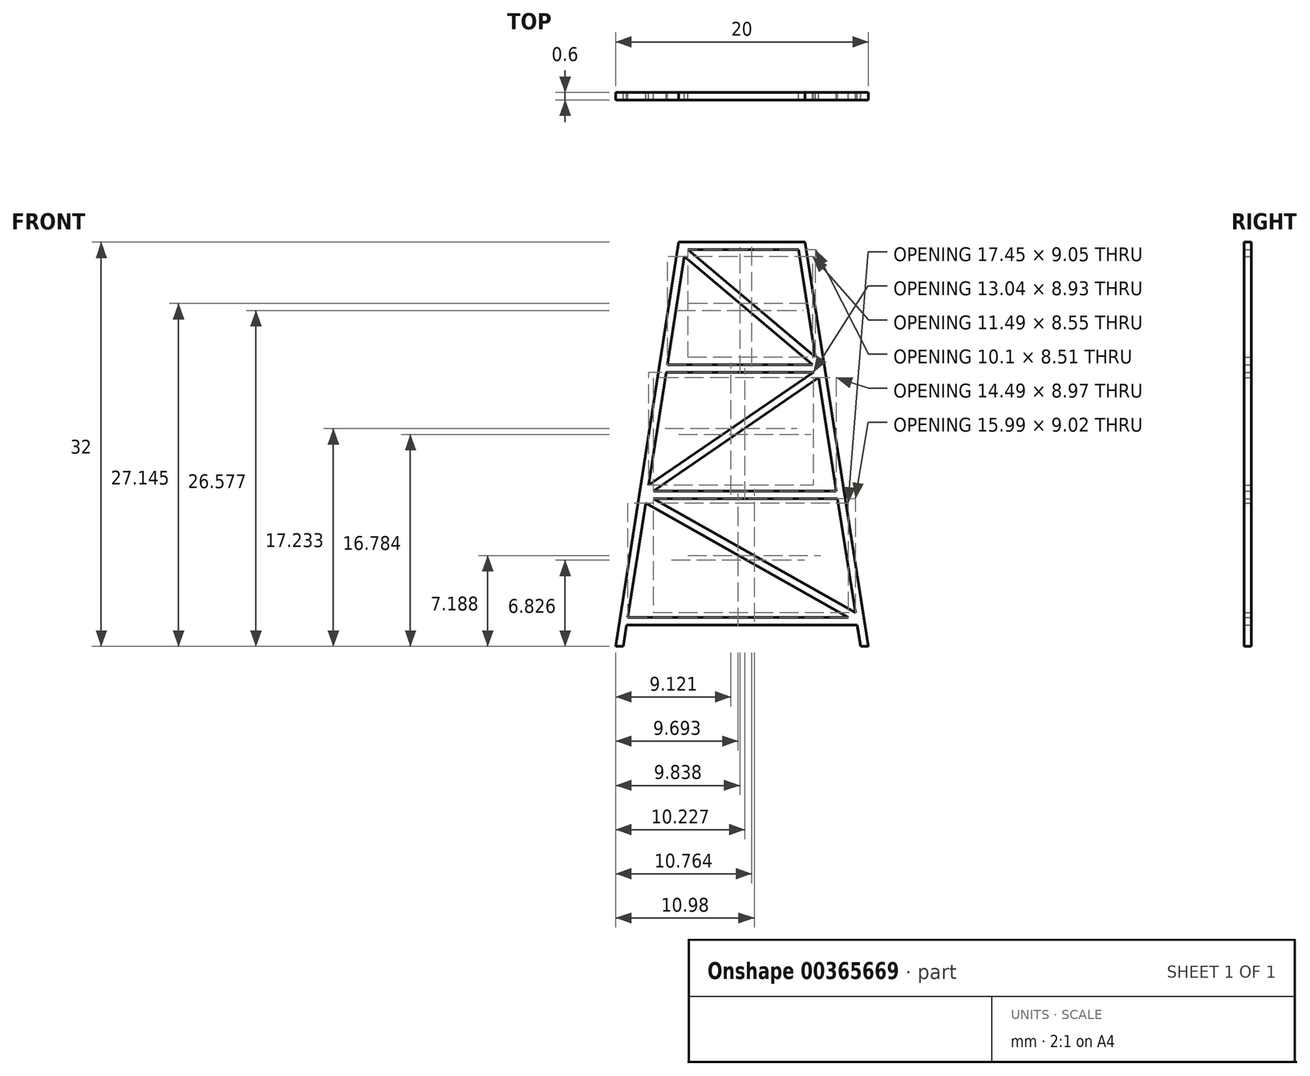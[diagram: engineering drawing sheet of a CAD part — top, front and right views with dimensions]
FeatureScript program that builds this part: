
annotation { "Feature Type Name" : "Feature", "Feature Type Description" : "" }
export const myFeature = defineFeature(function(context is Context, id is Id, definition is map)
    precondition{}
    {
        {
            var Q0;
            Q0=qCreatedBy(makeId("Front.planeOp"),FACE);
            var sketch = newSketch(context, id + "F0", { "sketchPlane" : qUnion([Q0])});
            skLineSegment(sketch, "E0", {"start": v(0, 0) * mm, "end": v(0, 32) * mm});
            skLineSegment(sketch, "E1", {"start": v(0, 32) * mm, "end": v(5, 32) * mm});
            skPoint(sketch, "E2", {"position": v(0, 0) * mm});
            skPoint(sketch, "E3", {"position": v(10, 0) * mm});
            skLineSegment(sketch, "E4", {"start": v(5, 32) * mm, "end": v(10, 0) * mm});
            skLineSegment(sketch, "E5", {"start": v(0, 31.4) * mm, "end": v(4.49, 31.4) * mm});
            skLineSegment(sketch, "E6", {"start": v(4.49, 31.4) * mm, "end": v(9.4, 0) * mm});
            skPoint(sketch, "E7", {"position": v(0, 2) * mm});
            skPoint(sketch, "E8", {"position": v(0, 12) * mm});
            skPoint(sketch, "E9", {"position": v(0, 22) * mm});
            skPoint(sketch, "E10", {"position": v(0, 22.3) * mm});
            skPoint(sketch, "E11", {"position": v(0, 21.7) * mm});
            skPoint(sketch, "E12", {"position": v(0, 12.3) * mm});
            skPoint(sketch, "E13", {"position": v(0, 11.7) * mm});
            skPoint(sketch, "E14", {"position": v(0, 2.3) * mm});
            skPoint(sketch, "E15", {"position": v(0, 1.7) * mm});
            skLineSegment(sketch, "E16", {"start": v(0, 22.3) * mm, "end": v(6.52, 22.3) * mm});
            skLineSegment(sketch, "E17", {"start": v(0, 21.7) * mm, "end": v(6, 21.7) * mm});
            skLineSegment(sketch, "E18", {"start": v(0, 12.3) * mm, "end": v(8.08, 12.3) * mm});
            skLineSegment(sketch, "E19", {"start": v(0, 11.7) * mm, "end": v(7.56, 11.7) * mm});
            skLineSegment(sketch, "E20", {"start": v(0, 2.3) * mm, "end": v(9.64, 2.3) * mm});
            skLineSegment(sketch, "E21", {"start": v(0, 1.7) * mm, "end": v(9.13, 1.7) * mm});
            skLineSegment(sketch, "E22.MirrorCS", {"start": v(0, 31.4) * mm, "end": v(-4.49, 31.4) * mm});
            skLineSegment(sketch, "E23.MirrorCS", {"start": v(0, 32) * mm, "end": v(-5, 32) * mm});
            skLineSegment(sketch, "E24.MirrorCS", {"start": v(-4.49, 31.4) * mm, "end": v(-9.4, 0) * mm});
            skLineSegment(sketch, "E25.MirrorCS", {"start": v(-5, 32) * mm, "end": v(-10, 0) * mm});
            skLineSegment(sketch, "E26.MirrorCS", {"start": v(0, 22.3) * mm, "end": v(-6.52, 22.3) * mm});
            skLineSegment(sketch, "E27.MirrorCS", {"start": v(0, 21.7) * mm, "end": v(-6, 21.7) * mm});
            skLineSegment(sketch, "E28.MirrorCS", {"start": v(0, 12.3) * mm, "end": v(-8.08, 12.3) * mm});
            skLineSegment(sketch, "E29.MirrorCS", {"start": v(0, 11.7) * mm, "end": v(-7.56, 11.7) * mm});
            skLineSegment(sketch, "E30.MirrorCS", {"start": v(0, 2.3) * mm, "end": v(-9.64, 2.3) * mm});
            skLineSegment(sketch, "E31.MirrorCS", {"start": v(0, 1.7) * mm, "end": v(-9.13, 1.7) * mm});
            skLineSegment(sketch, "E32", {"start": v(-5, 32) * mm, "end": v(6.52, 22.3) * mm});
            skLineSegment(sketch, "E33", {"start": v(-4.57, 30.85) * mm, "end": v(5.58, 22.3) * mm});
            skLineSegment(sketch, "E34", {"start": v(6.52, 22.3) * mm, "end": v(-8.08, 12.3) * mm});
            skLineSegment(sketch, "E35", {"start": v(-8.08, 12.3) * mm, "end": v(9.64, 2.3) * mm});
            skLineSegment(sketch, "E36", {"start": v(6.07, 21.27) * mm, "end": v(-7.02, 12.3) * mm});
            skLineSegment(sketch, "E37", {"start": v(-7.62, 11.35) * mm, "end": v(8.42, 2.3) * mm});
            skLineSegment(sketch, "E38", {"start": v(9.4, 0) * mm, "end": v(10, 0) * mm});
            skLineSegment(sketch, "E39", {"start": v(-10, 0) * mm, "end": v(-9.4, 0) * mm});
            skSolve(sketch);
        }
        {
            var Q0;
            {var subQ0=sQuery(id+"F0.wireOp",EDGE,"E39");Q0=makeQuery(id+"F0.imprint","IMPRINT",FACE,{"disambiguationData":[TD([[makeQuery(id+"F0.imprint","IMPRINT",EDGE,{"derivedFrom":subQ0}),1.0]])]});}
            var Q1;
            {var subQ5=sQuery(id+"F0.wireOp",EDGE,"E24.MirrorCS");var subQ8=makeQuery(id+"F0.imprint","INTERSECT",VERTEX,{"derivedFrom":[subQ5,sQuery(id+"F0.wireOp",EDGE,"E29.MirrorCS")]});Q1=makeQuery(id+"F0.imprint","IMPRINT",FACE,{"disambiguationData":[TD([[makeQuery(id+"F0.imprint","IMPRINT",EDGE,{"disambiguationData":[TD([[subQ8,1.0]])],"derivedFrom":subQ5}),-1.0]])]});}
            var Q2;
            {var subQ3=sQuery(id+"F0.wireOp",EDGE,"E24.MirrorCS");var subQ5=makeQuery(id+"F0.imprint","INTERSECT",VERTEX,{"derivedFrom":[subQ3,sQuery(id+"F0.wireOp",EDGE,"E27.MirrorCS")]});Q2=makeQuery(id+"F0.imprint","IMPRINT",FACE,{"disambiguationData":[TD([[makeQuery(id+"F0.imprint","IMPRINT",EDGE,{"disambiguationData":[TD([[subQ5,1.0]])],"derivedFrom":subQ3}),-1.0]])]});}
            var Q3;
            {var subQ5=sQuery(id+"F0.wireOp",EDGE,"E24.MirrorCS");var subQ6=sQuery(id+"F0.wireOp",EDGE,"E22.MirrorCS");var subQ7=makeQuery(id+"F0.imprint","INTERSECT",VERTEX,{"derivedFrom":[subQ6,subQ5]});Q3=makeQuery(id+"F0.imprint","IMPRINT",FACE,{"disambiguationData":[TD([[makeQuery(id+"F0.imprint","IMPRINT",EDGE,{"disambiguationData":[TD([[subQ7,1.0]])],"derivedFrom":subQ6}),-1.0]])]});}
            var Q4;
            {var subQ1=sQuery(id+"F0.wireOp",EDGE,"E1");Q4=makeQuery(id+"F0.imprint","IMPRINT",FACE,{"disambiguationData":[TD([[makeQuery(id+"F0.imprint","IMPRINT",EDGE,{"derivedFrom":subQ1}),-1.0]])]});}
            var Q5;
            {var subQ0=sQuery(id+"F0.wireOp",EDGE,"E23.MirrorCS");Q5=makeQuery(id+"F0.imprint","IMPRINT",FACE,{"disambiguationData":[TD([[makeQuery(id+"F0.imprint","IMPRINT",EDGE,{"derivedFrom":subQ0}),1.0]])]});}
            var Q6;
            {var subQ0=sQuery(id+"F0.wireOp",EDGE,"E6");var subQ4=makeQuery(id+"F0.imprint","INTERSECT",VERTEX,{"derivedFrom":[subQ0,sQuery(id+"F0.wireOp",EDGE,"E17")]});Q6=makeQuery(id+"F0.imprint","IMPRINT",FACE,{"disambiguationData":[TD([[makeQuery(id+"F0.imprint","IMPRINT",EDGE,{"disambiguationData":[TD([[subQ4,1.0]])],"derivedFrom":subQ0}),1.0]])]});}
            var Q7;
            {var subQ0=sQuery(id+"F0.wireOp",EDGE,"E6");var subQ1=makeQuery(id+"F0.imprint","INTERSECT",VERTEX,{"derivedFrom":[subQ0,sQuery(id+"F0.wireOp",EDGE,"E19")]});Q7=makeQuery(id+"F0.imprint","IMPRINT",FACE,{"disambiguationData":[TD([[makeQuery(id+"F0.imprint","IMPRINT",EDGE,{"disambiguationData":[TD([[subQ1,1.0]])],"derivedFrom":subQ0}),1.0]])]});}
            var Q8;
            {var subQ5=sQuery(id+"F0.wireOp",EDGE,"E38");Q8=makeQuery(id+"F0.imprint","IMPRINT",FACE,{"disambiguationData":[TD([[makeQuery(id+"F0.imprint","IMPRINT",EDGE,{"derivedFrom":subQ5}),1.0]])]});}
            var Q9;
            {var subQ4=sQuery(id+"F0.wireOp",EDGE,"E21");Q9=makeQuery(id+"F0.imprint","IMPRINT",FACE,{"disambiguationData":[TD([[makeQuery(id+"F0.imprint","IMPRINT",EDGE,{"derivedFrom":subQ4}),1.0]])]});}
            var Q10;
            {var subQ3=sQuery(id+"F0.wireOp",EDGE,"E31.MirrorCS");Q10=makeQuery(id+"F0.imprint","IMPRINT",FACE,{"disambiguationData":[TD([[makeQuery(id+"F0.imprint","IMPRINT",EDGE,{"derivedFrom":subQ3}),-1.0]])]});}
            var Q11;
            {var subQ1=sQuery(id+"F0.wireOp",EDGE,"E0");var subQ5=sQuery(id+"F0.wireOp",EDGE,"E37");var subQ9=makeQuery(id+"F0.imprint","INTERSECT",VERTEX,{"derivedFrom":[subQ1,subQ5]});Q11=makeQuery(id+"F0.imprint","IMPRINT",FACE,{"disambiguationData":[TD([[makeQuery(id+"F0.imprint","IMPRINT",EDGE,{"disambiguationData":[TD([[subQ9,-1.0]])],"derivedFrom":subQ1}),-1.0]])]});}
            var Q12;
            {var subQ1=sQuery(id+"F0.wireOp",EDGE,"E0");var subQ7=sQuery(id+"F0.wireOp",EDGE,"E37");var subQ9=makeQuery(id+"F0.imprint","INTERSECT",VERTEX,{"derivedFrom":[subQ1,subQ7]});Q12=makeQuery(id+"F0.imprint","IMPRINT",FACE,{"disambiguationData":[TD([[makeQuery(id+"F0.imprint","IMPRINT",EDGE,{"disambiguationData":[TD([[subQ9,-1.0]])],"derivedFrom":subQ1}),1.0]])]});}
            var Q13;
            {var subQ3=sQuery(id+"F0.wireOp",EDGE,"E19");Q13=makeQuery(id+"F0.imprint","IMPRINT",FACE,{"disambiguationData":[TD([[makeQuery(id+"F0.imprint","IMPRINT",EDGE,{"derivedFrom":subQ3}),1.0]])]});}
            var Q14;
            {var subQ0=sQuery(id+"F0.wireOp",EDGE,"E28.MirrorCS");var subQ4=sQuery(id+"F0.wireOp",EDGE,"E24.MirrorCS");var subQ5=makeQuery(id+"F0.imprint","INTERSECT",VERTEX,{"derivedFrom":[subQ4,subQ0]});Q14=makeQuery(id+"F0.imprint","IMPRINT",FACE,{"disambiguationData":[TD([[makeQuery(id+"F0.imprint","IMPRINT",EDGE,{"disambiguationData":[TD([[subQ5,-1.0]])],"derivedFrom":subQ4}),1.0]])]});}
            var Q15;
            {var subQ1=sQuery(id+"F0.wireOp",EDGE,"E0");var subQ7=sQuery(id+"F0.wireOp",EDGE,"E36");var subQ9=makeQuery(id+"F0.imprint","INTERSECT",VERTEX,{"derivedFrom":[subQ1,subQ7]});Q15=makeQuery(id+"F0.imprint","IMPRINT",FACE,{"disambiguationData":[TD([[makeQuery(id+"F0.imprint","IMPRINT",EDGE,{"disambiguationData":[TD([[subQ9,-1.0]])],"derivedFrom":subQ1}),-1.0]])]});}
            var Q16;
            {var subQ1=sQuery(id+"F0.wireOp",EDGE,"E0");var subQ5=sQuery(id+"F0.wireOp",EDGE,"E36");var subQ9=makeQuery(id+"F0.imprint","INTERSECT",VERTEX,{"derivedFrom":[subQ1,subQ5]});Q16=makeQuery(id+"F0.imprint","IMPRINT",FACE,{"disambiguationData":[TD([[makeQuery(id+"F0.imprint","IMPRINT",EDGE,{"disambiguationData":[TD([[subQ9,-1.0]])],"derivedFrom":subQ1}),1.0]])]});}
            var Q17;
            {var subQ1=sQuery(id+"F0.wireOp",EDGE,"E0");var subQ5=sQuery(id+"F0.wireOp",EDGE,"E33");var subQ9=makeQuery(id+"F0.imprint","INTERSECT",VERTEX,{"derivedFrom":[subQ1,subQ5]});Q17=makeQuery(id+"F0.imprint","IMPRINT",FACE,{"disambiguationData":[TD([[makeQuery(id+"F0.imprint","IMPRINT",EDGE,{"disambiguationData":[TD([[subQ9,-1.0]])],"derivedFrom":subQ1}),-1.0]])]});}
            var Q18;
            {var subQ1=sQuery(id+"F0.wireOp",EDGE,"E0");var subQ7=sQuery(id+"F0.wireOp",EDGE,"E33");var subQ8=makeQuery(id+"F0.imprint","INTERSECT",VERTEX,{"derivedFrom":[subQ1,subQ7]});Q18=makeQuery(id+"F0.imprint","IMPRINT",FACE,{"disambiguationData":[TD([[makeQuery(id+"F0.imprint","IMPRINT",EDGE,{"disambiguationData":[TD([[subQ8,-1.0]])],"derivedFrom":subQ1}),1.0]])]});}
            var Q19;
            {var subQ0=sQuery(id+"F0.wireOp",EDGE,"E16");var subQ6=sQuery(id+"F0.wireOp",EDGE,"E6");var subQ7=makeQuery(id+"F0.imprint","INTERSECT",VERTEX,{"derivedFrom":[subQ6,subQ0]});Q19=makeQuery(id+"F0.imprint","IMPRINT",FACE,{"disambiguationData":[TD([[makeQuery(id+"F0.imprint","IMPRINT",EDGE,{"disambiguationData":[TD([[subQ7,-1.0]])],"derivedFrom":subQ6}),-1.0]])]});}
            var Q20;
            {var subQ3=sQuery(id+"F0.wireOp",EDGE,"E27.MirrorCS");Q20=makeQuery(id+"F0.imprint","IMPRINT",FACE,{"disambiguationData":[TD([[makeQuery(id+"F0.imprint","IMPRINT",EDGE,{"derivedFrom":subQ3}),-1.0]])]});}
            var Q21;
            {var subQ0=sQuery(id+"F0.wireOp",EDGE,"E32");var subQ1=sQuery(id+"F0.wireOp",EDGE,"E6");var subQ2=makeQuery(id+"F0.imprint","INTERSECT",VERTEX,{"derivedFrom":[subQ1,subQ0]});Q21=makeQuery(id+"F0.imprint","IMPRINT",FACE,{"disambiguationData":[TD([[makeQuery(id+"F0.imprint","IMPRINT",EDGE,{"disambiguationData":[TD([[subQ2,-1.0]])],"derivedFrom":subQ1}),1.0]])]});}
            var Q22;
            {var subQ0=sQuery(id+"F0.wireOp",EDGE,"E16");var subQ1=sQuery(id+"F0.wireOp",EDGE,"E6");var subQ2=makeQuery(id+"F0.imprint","INTERSECT",VERTEX,{"derivedFrom":[subQ1,subQ0]});Q22=makeQuery(id+"F0.imprint","IMPRINT",FACE,{"disambiguationData":[TD([[makeQuery(id+"F0.imprint","IMPRINT",EDGE,{"disambiguationData":[TD([[subQ2,-1.0]])],"derivedFrom":subQ1}),1.0]])]});}
            var Q23;
            {var subQ0=sQuery(id+"F0.wireOp",EDGE,"E17");var subQ1=sQuery(id+"F0.wireOp",EDGE,"E6");var subQ2=makeQuery(id+"F0.imprint","INTERSECT",VERTEX,{"derivedFrom":[subQ1,subQ0]});Q23=makeQuery(id+"F0.imprint","IMPRINT",FACE,{"disambiguationData":[TD([[makeQuery(id+"F0.imprint","IMPRINT",EDGE,{"disambiguationData":[TD([[subQ2,1.0]])],"derivedFrom":subQ1}),-1.0]])]});}
            var Q24;
            {var subQ0=sQuery(id+"F0.wireOp",EDGE,"E35");var subQ1=sQuery(id+"F0.wireOp",EDGE,"E6");var subQ2=makeQuery(id+"F0.imprint","INTERSECT",VERTEX,{"derivedFrom":[subQ1,subQ0]});Q24=makeQuery(id+"F0.imprint","IMPRINT",FACE,{"disambiguationData":[TD([[makeQuery(id+"F0.imprint","IMPRINT",EDGE,{"disambiguationData":[TD([[subQ2,-1.0]])],"derivedFrom":subQ1}),1.0]])]});}
            var Q25;
            {var subQ0=sQuery(id+"F0.wireOp",EDGE,"E34");var subQ1=sQuery(id+"F0.wireOp",EDGE,"E24.MirrorCS");var subQ2=makeQuery(id+"F0.imprint","INTERSECT",VERTEX,{"derivedFrom":[subQ1,subQ0]});Q25=makeQuery(id+"F0.imprint","IMPRINT",FACE,{"disambiguationData":[TD([[makeQuery(id+"F0.imprint","IMPRINT",EDGE,{"disambiguationData":[TD([[subQ2,-1.0]])],"derivedFrom":subQ1}),-1.0]])]});}
            var Q26;
            {var subQ0=sQuery(id+"F0.wireOp",EDGE,"E28.MirrorCS");var subQ1=sQuery(id+"F0.wireOp",EDGE,"E24.MirrorCS");var subQ2=makeQuery(id+"F0.imprint","INTERSECT",VERTEX,{"derivedFrom":[subQ1,subQ0]});Q26=makeQuery(id+"F0.imprint","IMPRINT",FACE,{"disambiguationData":[TD([[makeQuery(id+"F0.imprint","IMPRINT",EDGE,{"disambiguationData":[TD([[subQ2,-1.0]])],"derivedFrom":subQ1}),-1.0]])]});}
            var Q27;
            {var subQ0=sQuery(id+"F0.wireOp",EDGE,"E29.MirrorCS");var subQ1=sQuery(id+"F0.wireOp",EDGE,"E24.MirrorCS");var subQ2=makeQuery(id+"F0.imprint","INTERSECT",VERTEX,{"derivedFrom":[subQ1,subQ0]});Q27=makeQuery(id+"F0.imprint","IMPRINT",FACE,{"disambiguationData":[TD([[makeQuery(id+"F0.imprint","IMPRINT",EDGE,{"disambiguationData":[TD([[subQ2,1.0]])],"derivedFrom":subQ1}),1.0]])]});}
            extrude(context, id + "F1", {"entities" : qUnion([Q0, Q1, Q2, Q3, Q4, Q5, Q6, Q7, Q8, Q9, Q10, Q11, Q12, Q13, Q14, Q15, Q16, Q17, Q18, Q19, Q20, Q21, Q22, Q23, Q24, Q25, Q26, Q27]), "depth" : 0.6 * mm});
        }
    });
